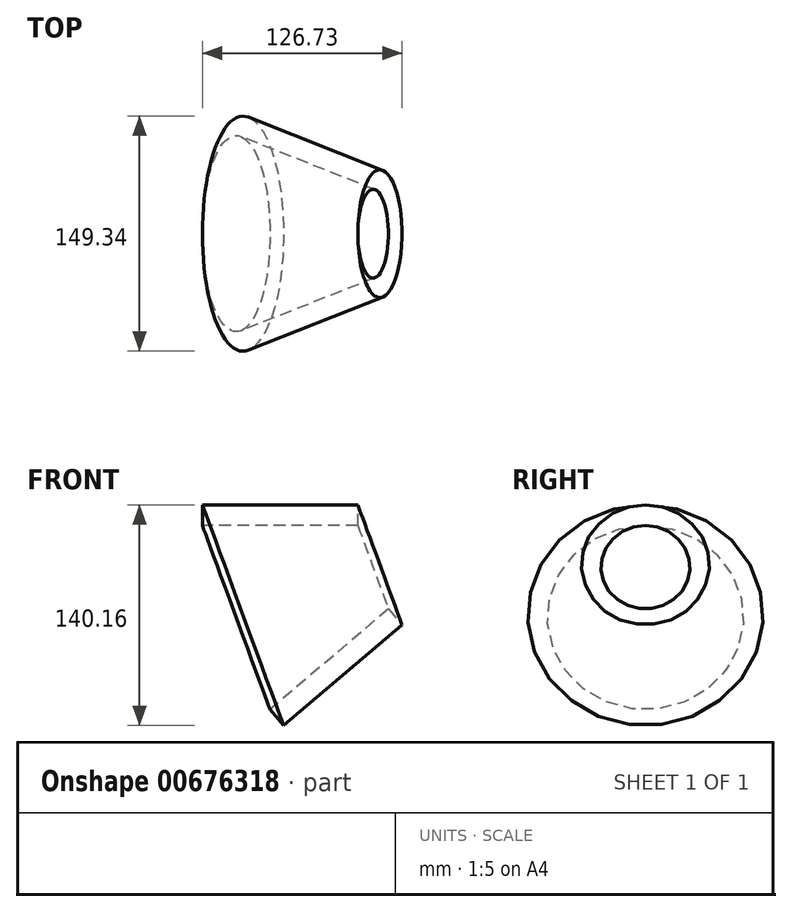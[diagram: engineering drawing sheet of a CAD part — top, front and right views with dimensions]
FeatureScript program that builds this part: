
annotation { "Feature Type Name" : "Feature", "Feature Type Description" : "" }
export const myFeature = defineFeature(function(context is Context, id is Id, definition is map)
    precondition{}
    {
        {
            var Q0;
            Q0=qCreatedBy(makeId("Front.planeOp"),FACE);
            var sketch = newSketch(context, id + "F0", { "sketchPlane" : qUnion([Q0])});
            skLineSegment(sketch, "E0.bottom", {"start": v(-58.2, 42.15) * mm, "end": v(40.5, 42.15) * mm});
            skLineSegment(sketch, "E0.top", {"start": v(-58.2, 28.94) * mm, "end": v(40.5, 28.94) * mm});
            skLineSegment(sketch, "E0.left", {"start": v(-58.2, 42.15) * mm, "end": v(-58.2, 28.94) * mm});
            skLineSegment(sketch, "E0.right", {"start": v(40.5, 42.15) * mm, "end": v(40.5, 28.94) * mm});
            skLineSegment(sketch, "E1", {"start": v(-65.1, -39.95) * mm, "end": v(63.9, 7.5) * mm, "construction": true});
            skSolve(sketch);
        }
        {
            var Q0;
            Q0=makeQuery(id+"F0.imprint","IMPRINT",FACE,{"disambiguationData":[TD([[makeQuery(id+"F0.imprint","IMPRINT",EDGE,{"derivedFrom":sQuery(id+"F0.wireOp",EDGE,"E0.bottom")}),-1.0]])]});
            var Q1;
            Q1=sQuery(id+"F0.wireOp",EDGE,"E1");
            revolve(context, id + "F1", {"entities" : qUnion([Q0]), "axis" : qUnion([Q1]), "revolveType" : RevolveType.FULL});
        }
    });
